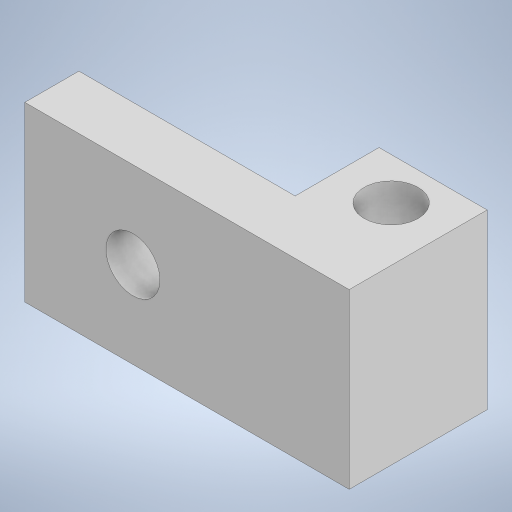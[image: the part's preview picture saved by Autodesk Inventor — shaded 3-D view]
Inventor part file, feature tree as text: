
AUTODESK INVENTOR PART (.ipt)
format: ipt  version: 2023 (Build 270158000, 158)  size: 269,312 bytes
history: native  units: in
note: dims shown in document units (in); Inventor stores cm internally (conversion verified against a paired STEP export)
features: extrude x3, sketch x3
ambient origin geometry x8: Origin, YZ Plane, XZ Plane, XY Plane, X Axis, Y Axis, Z Axis, Center Point
bodies: Solid1 (feature_tree)
feature tree (6):
  extrude  "Extrusion1"  Depth=0.6299in
  extrude  "Extrusion2"  Depth=0.3937in
  extrude  "Extrusion3"  Depth=0.1969in TaperAngle=0.0deg
  sketch  "Sketch1"  dims[d0=0.7874in d1=0.6299in]
  sketch  "Sketch2"  dims[d2=0.315in d3=0.3937in]
  sketch  "Sketch3"  dims[d4=0.1969in d5=0.1969in d6=0.0in d7=0.3937in d8=0.3055in d9=0.1969in d10=0.6299in d11=0.0in d12=0.3543in d13=0.0in]
